# Revit family: ASH_ArmitageShanks_CounterTopWashBasins_Sandringham21-50cm
name_source: partatom
category: Plumbing Fixtures
revit_build: Autodesk Revit MEP 2012 (Build: 20110309_2315(x64)
units: mm (PartAtom-declared; Revit-internal decimal feet)

## types (3) — shared parameters
Accessories = www.idealspec.co.uk
AreaUnits = millimeters
Assembly Code = C1030200
AssetType = Fixed
Brand = Armitage Shanks
Category = SanitaryTerminal_WASHHANDBASIN_UK
Color = White
ConnectionType = Plumbing
Default Elevation = 1219 mm
DrainSize = 32 mm  [stored 0.104987 ft]
DurationUnit = year
ECA = No
ExpectedLife = 30
Finish = White
IfcExportAs = IfcSanitaryTerminalType
IfcExportType = WASHHANDBASIN
InstallationInstructions = www.idealspec.co.uk/resources.html
LinearUnits = millimeters
ManufacturerURL = www.idealspec.co.uk
Material = Vitreous china
NBSDescription = Counter top wash basins
NBSReference = 45-35-70/360
NettWeight = 7 Kg
NominalDepth = 430 mm
NominalHeight = 185 mm  [stored 0.606955 ft]
NominalLength = 430 mm
NominalWidth = 500 mm
Shape = Sculptured
Size = 500 x 430 x 185 mm
Space = Internal
SpareParts = www.fastpart-spares.co.uk
URL = www.idealspec.co.uk
Uniclass2 = Pr_40_20_96_18
Version = 1
VolumeUnits = Litres
WRAS = No
WarrantyDescription = Manufacturers warranty
WarrantyDurationParts = 99
WarrantyDurationUnit = year
WashHandBasinMounting = CounterTop
WashHandBasinType = HANDRINSE
WaterEfficientProduct = No
zero-valued in all types: CWFU, HWFU, WFU

## per-type parameters (varying)
| type | BIMObjectName | Description | E8952-1Th | E8953-2Th | Features | Model | ModelNumber | ModelReference | Name | ProductInformation |
| E895201-Sandringham 21 countertop washbasin 50cm, 1 taphole with overflow, no chainstay hole | ASH_ArmitageShanks_CounterTopWashBasins_Sandringham21_E8952 | Sandringham 21 countertop washbasin 50 cm, 1 taphole with overflow, no chainstay hole | Yes | No | Countertop washbasin 50 cm, 1 taphole with overflow, no chainstay hole | E895201 | E895201 | Sandringham 21 countertop washbasin 50 cm, 1 taphole with overflow, no chainstay hole | CounterTopWashBasins_Sandringham21_E8952_ArmitageShanks | www.idealspec.co.uk/assets/datasheet/E895201 |
| E895301-Sandringham 21 countertop washbasin 50cm, 2 tapholes with overflow and chainstay hole | ASH_ArmitageShanks_CounterTopWashBasins_Sandringham21_E8953 | Sandringham 21 countertop washbasin 50 cm, 2 tapholes with overflow and chainstay hole | No | Yes | Countertop washbasin 50 cm, 2 tapholes with overflow and chainstay hole | E895301 | E895301 | Sandringham 21 countertop washbasin 50 cm, 2 tapholes with overflow and chainstay hole | CounterTopWashBasins_Sandringham21_E8953_ArmitageShanks | www.idealspec.co.uk/assets/datasheet/E895301 |
| E8954-Sandringham 21 countertop washbasin 50cm, 2 tapholes with overflow, no chainstay hole | ASH_ArmitageShanks_CounterTopWashBasins_Sandringham21_E8954 | Sandringham 21 countertop washbasin 50 cm, 2 tapholes with overflow, no chainstay hole | No | Yes | Countertop washbasin 50 cm, 2 tapholes with overflow, no chainstay hole | E895401 | E895401 | Sandringham 21 countertop washbasin 50 cm, 2 tapholes with overflow, no chainstay hole | CounterTopWashBasins_Sandringham21_E8954_ArmitageShanks | www.idealspec.co.uk/assets/datasheet/E895401 |

note: [stored X ft] marks values corroborated as IEEE doubles in the binary element streams (Revit-internal decimal feet)

## geometry (parser evidence)
native form markers: Blend x1, Sweep x12
no freeform markers — native parametric forms only
